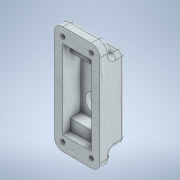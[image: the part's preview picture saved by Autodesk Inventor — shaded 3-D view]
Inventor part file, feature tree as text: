
AUTODESK INVENTOR PART (.ipt)
format: ipt  version: 2021 (Build 250183000, 183)  size: 274,944 bytes
history: native  units: mm
features: extrude x7, sketch x7, fillet x3
ambient origin geometry x8: Origin, YZ Plane, XZ Plane, XY Plane, X Axis, Y Axis, Z Axis, Center Point
bodies: Solid1 (feature_tree)
feature tree (17):
  extrude  "Extrusion1"  Depth=76.0mm
  fillet  "Fillet1"  Radius=18.0mm
  extrude  "Extrusion2"  Depth=20.0mm
  extrude  "Extrusion3"  Depth=18.0mm
  extrude  "Extrusion4"  Depth=12.5mm TaperAngle=0.0deg
  extrude  "Extrusion5"  Depth=10.0mm
  fillet  "Fillet2"  Radius=10.0mm
  extrude  "Extrusion6"  Depth=7.7mm
  extrude  "Extrusion7"  Depth=2.0mm
  fillet  "Fillet3"  Radius=5.0mm
  sketch  "Sketch1"  dims[d0=32.0mm d1=76.0mm d2=18.0mm d3=0.0mm]
  sketch  "Sketch2"  dims[d4=6.0mm d5=20.0mm]
  sketch  "Sketch3"  dims[d6=40.0mm d7=18.0mm]
  sketch  "Sketch4"  dims[d8=6.0mm d9=12.5mm d10=0.0mm]
  sketch  "Sketch5"  dims[d11=13.5mm d12=10.0mm d13=10.0mm]
  sketch  "Sketch6"  dims[d14=12.5mm d15=0.0mm d16=7.7mm]
  sketch  "Sketch7"  dims[d17=20.0mm d18=7.7mm d19=5.0mm d20=0.0mm d21=10.0mm d22=10.0mm d23=10.0mm d24=10.0mm d25=5.0mm d26=0.0mm d27=3.0mm d28=3.0mm d29=3.0mm d30=3.0mm d31=3.0mm d32=5.0mm d33=10.0mm d34=0.0mm d35=0.0mm d36=22.0mm d37=2.0mm d38=0.0mm d39=2.0mm]
